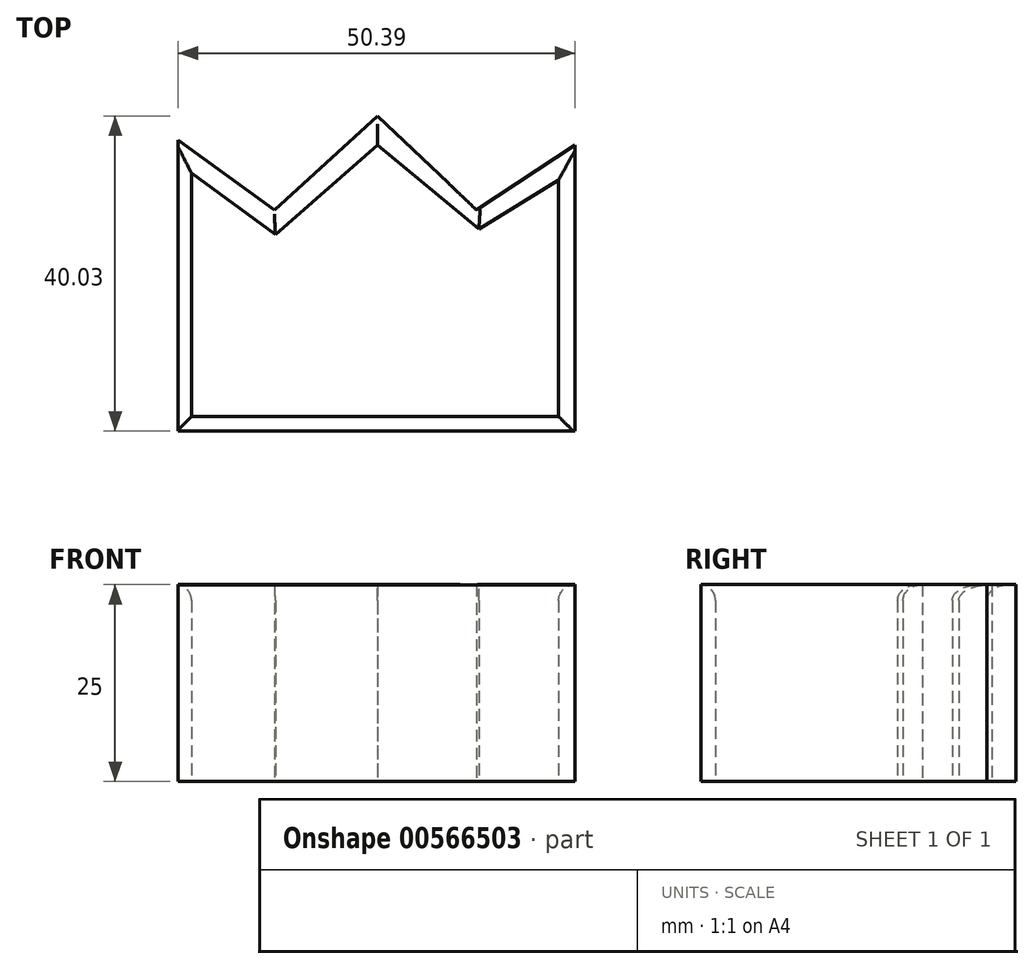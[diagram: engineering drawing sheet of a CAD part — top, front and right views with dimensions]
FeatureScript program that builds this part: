
annotation { "Feature Type Name" : "Feature", "Feature Type Description" : "" }
export const myFeature = defineFeature(function(context is Context, id is Id, definition is map)
    precondition{}
    {
        {
            var Q0;
            Q0=qCreatedBy(makeId("Top.planeOp"),FACE);
            var sketch = newSketch(context, id + "F0", { "sketchPlane" : qUnion([Q0])});
            skLineSegment(sketch, "E0", {"start": v(-25.35, 0) * mm, "end": v(-25.35, 20.77) * mm});
            skLineSegment(sketch, "E1", {"start": v(25.04, 0) * mm, "end": v(25.04, 20.16) * mm});
            skLineSegment(sketch, "E2", {"start": v(0, 23.82) * mm, "end": v(12.52, 11.9) * mm});
            skLineSegment(sketch, "E3", {"start": v(25.04, 20.16) * mm, "end": v(12.52, 11.9) * mm});
            skLineSegment(sketch, "E4", {"start": v(-13.13, 11.9) * mm, "end": v(0, 23.82) * mm});
            skLineSegment(sketch, "E5", {"start": v(-25.35, 20.77) * mm, "end": v(-13.13, 11.9) * mm});
            skLineSegment(sketch, "E6", {"start": v(25.04, 0) * mm, "end": v(25.04, -16.21) * mm});
            skLineSegment(sketch, "E7", {"start": v(25.04, -16.21) * mm, "end": v(-25.35, -16.21) * mm});
            skLineSegment(sketch, "E8", {"start": v(-25.35, -16.21) * mm, "end": v(-25.35, 0) * mm});
            skLineSegment(sketch, "E9", {"start": v(-23.66, 16.56) * mm, "end": v(-23.66, -14.36) * mm});
            skLineSegment(sketch, "E10", {"start": v(-23.66, -14.36) * mm, "end": v(22.97, -14.36) * mm});
            skLineSegment(sketch, "E11", {"start": v(22.97, -14.36) * mm, "end": v(22.97, 15.72) * mm});
            skLineSegment(sketch, "E12", {"start": v(22.97, 15.72) * mm, "end": v(12.83, 9.46) * mm});
            skLineSegment(sketch, "E13", {"start": v(12.83, 9.46) * mm, "end": v(0, 20.16) * mm});
            skLineSegment(sketch, "E14", {"start": v(0, 20.16) * mm, "end": v(-13.01, 8.79) * mm});
            skLineSegment(sketch, "E15", {"start": v(-13.01, 8.79) * mm, "end": v(-23.66, 16.56) * mm});
            skSolve(sketch);
        }
        {
            var Q0;
            Q0=makeQuery(id+"F0.imprint","IMPRINT",FACE,{"disambiguationData":[TD([[makeQuery(id+"F0.imprint","IMPRINT",EDGE,{"derivedFrom":sQuery(id+"F0.wireOp",EDGE,"E0")}),-1.0]])]});
            var sketch = newSketch(context, id + "F1", { "sketchPlane" : qUnion([Q0])});
            skSolve(sketch);
        }
        {
            var Q0;
            Q0 = qSketchRegion(id + "F1", true);
            var Q1;
            Q1=makeQuery(id+"F0.imprint","IMPRINT",FACE,{"disambiguationData":[TD([[makeQuery(id+"F0.imprint","IMPRINT",EDGE,{"derivedFrom":sQuery(id+"F0.wireOp",EDGE,"E0")}),-1.0]])]});
            extrude(context, id + "F2", {"entities" : qUnion([Q0, Q1]), "depth" : 25 * mm, "offsetDistance" : 25 * mm});
        }
        {
            var Q0;
            Q0=makeQuery(id+"F2.opExtrude","CAP_EDGE",EDGE,{"disambiguationData":[OSD([sQuery(id+"F0.wireOp",EDGE,"E9")])],"isStart":false});
            var Q1;
            Q1=makeQuery(id+"F2.opExtrude","CAP_EDGE",EDGE,{"disambiguationData":[OSD([sQuery(id+"F0.wireOp",EDGE,"E15")])],"isStart":false});
            var Q2;
            Q2=makeQuery(id+"F2.opExtrude","CAP_EDGE",EDGE,{"disambiguationData":[OSD([sQuery(id+"F0.wireOp",EDGE,"E14")])],"isStart":false});
            var Q3;
            Q3=makeQuery(id+"F2.opExtrude","CAP_EDGE",EDGE,{"disambiguationData":[OSD([sQuery(id+"F0.wireOp",EDGE,"E13")])],"isStart":false});
            var Q4;
            Q4=makeQuery(id+"F2.opExtrude","CAP_EDGE",EDGE,{"disambiguationData":[OSD([sQuery(id+"F0.wireOp",EDGE,"E12")])],"isStart":false});
            var Q5;
            Q5=makeQuery(id+"F2.opExtrude","CAP_EDGE",EDGE,{"disambiguationData":[OSD([sQuery(id+"F0.wireOp",EDGE,"E10")])],"isStart":false});
            var Q6;
            Q6=makeQuery(id+"F2.opExtrude","CAP_EDGE",EDGE,{"disambiguationData":[OSD([sQuery(id+"F0.wireOp",EDGE,"E11")])],"isStart":false});
            fillet(context, id + "F3", {"entities" : qUnion([Q0, Q1, Q2, Q3, Q4, Q5, Q6]), "radius" : 2 * mm, "tangentPropagation" : true, "allowEdgeOverflow" : false});
        }
    });
